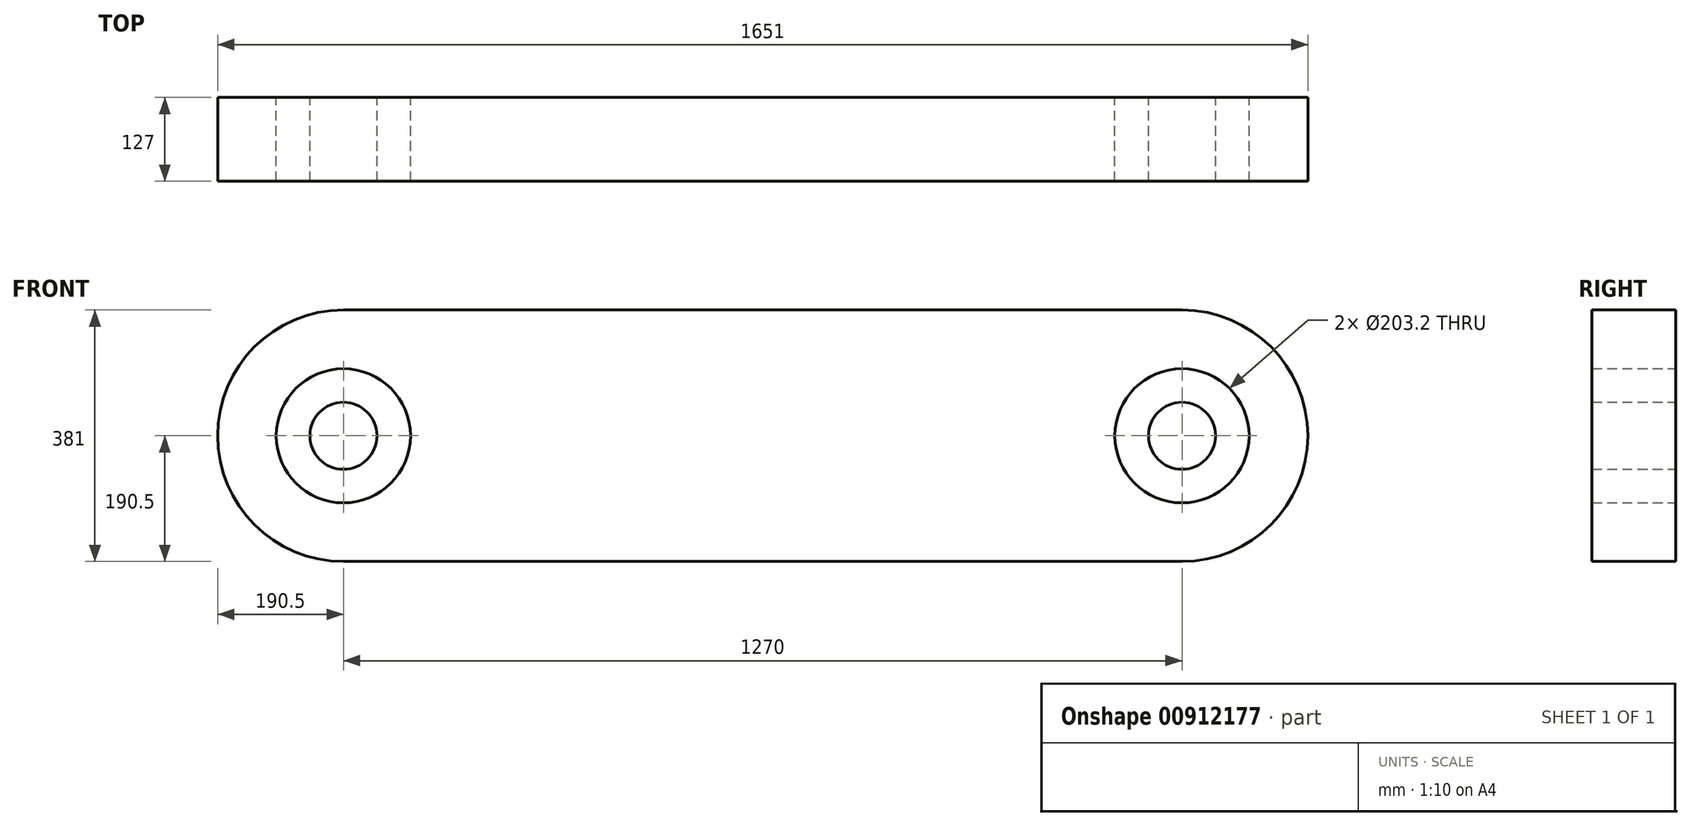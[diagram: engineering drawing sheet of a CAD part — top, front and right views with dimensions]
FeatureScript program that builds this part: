
annotation { "Feature Type Name" : "Feature", "Feature Type Description" : "" }
export const myFeature = defineFeature(function(context is Context, id is Id, definition is map)
    precondition{}
    {
        {
            var Q0;
            Q0=qCreatedBy(makeId("Front.planeOp"),FACE);
            var sketch = newSketch(context, id + "F0", { "sketchPlane" : qUnion([Q0])});
            skLineSegment(sketch, "E0.bottom", {"start": v(0, 0) * mm, "end": v(1270, 0) * mm});
            skLineSegment(sketch, "E0.top", {"start": v(0, 381) * mm, "end": v(1270, 381) * mm});
            skArc(sketch, "E1", {"start": v(0, 381) * mm, "mid": v(-190.5, 190.5) * mm, "end": v(0, 0) * mm});
            skArc(sketch, "E2", {"start": v(1270, 0) * mm, "mid": v(1460.5, 190.5) * mm, "end": v(1270, 381) * mm});
            skCircle(sketch, "E3", {"center": v(0, 190.5) * mm, "radius": 101.6 * mm});
            skCircle(sketch, "E4", {"center": v(0, 190.5) * mm, "radius": 50.8 * mm});
            skCircle(sketch, "E5", {"center": v(1270, 190.5) * mm, "radius": 101.6 * mm});
            skCircle(sketch, "E6", {"center": v(1270, 190.5) * mm, "radius": 50.8 * mm});
            skSolve(sketch);
        }
        {
            var Q0;
            Q0=makeQuery(id+"F0.imprint","IMPRINT",FACE,{"disambiguationData":[TD([[makeQuery(id+"F0.imprint","IMPRINT",EDGE,{"derivedFrom":sQuery(id+"F0.wireOp",EDGE,"E0.bottom")}),1.0]])]});
            var Q1;
            Q1=makeQuery(id+"F0.imprint","IMPRINT",FACE,{"disambiguationData":[TD([[makeQuery(id+"F0.imprint","IMPRINT",EDGE,{"derivedFrom":sQuery(id+"F0.wireOp",EDGE,"E4")}),1.0]])]});
            var Q2;
            Q2=makeQuery(id+"F0.imprint","IMPRINT",FACE,{"disambiguationData":[TD([[makeQuery(id+"F0.imprint","IMPRINT",EDGE,{"derivedFrom":sQuery(id+"F0.wireOp",EDGE,"E6")}),1.0]])]});
            extrude(context, id + "F1", {"entities" : qUnion([Q0, Q1, Q2]), "depth" : 127 * mm, "offsetDistance" : 25.4 * mm});
        }
    });
